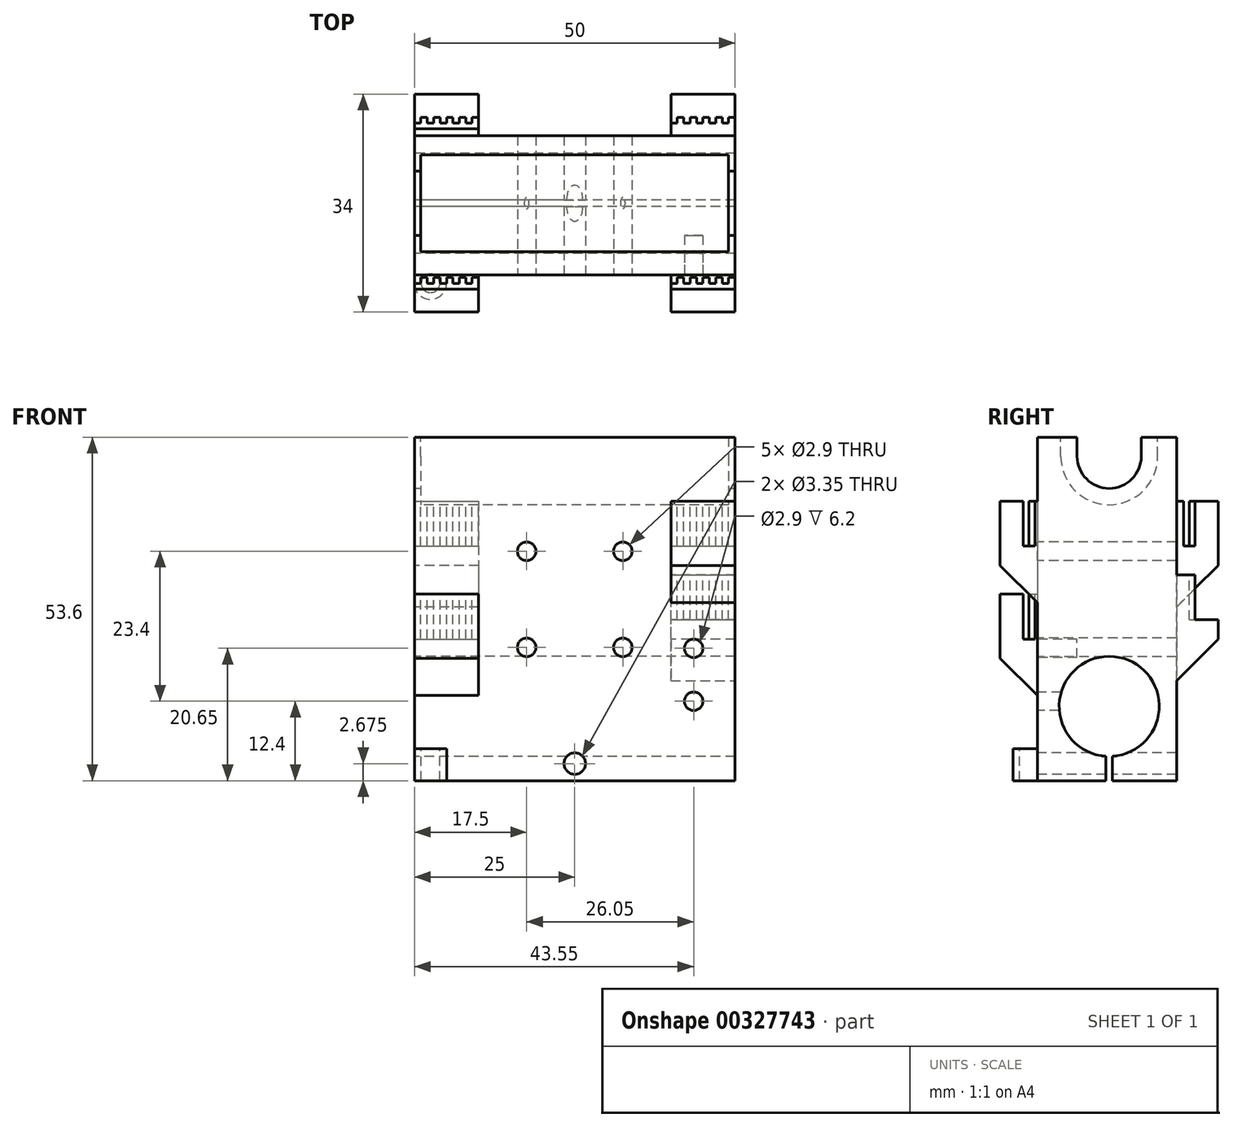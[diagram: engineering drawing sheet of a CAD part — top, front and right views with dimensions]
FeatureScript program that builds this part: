
annotation { "Feature Type Name" : "Feature", "Feature Type Description" : "" }
export const myFeature = defineFeature(function(context is Context, id is Id, definition is map)
    precondition{}
    {
        {
            var Q0;
            Q0=qCreatedBy(makeId("Top.planeOp"),FACE);
            var sketch = newSketch(context, id + "F0", { "sketchPlane" : qUnion([Q0])});
            skLineSegment(sketch, "E0.bottom", {"start": v(0, 0) * mm, "end": v(50, 0) * mm});
            skLineSegment(sketch, "E0.top", {"start": v(0, 20) * mm, "end": v(50, 20) * mm});
            skLineSegment(sketch, "E0.left", {"start": v(0, 0) * mm, "end": v(0, 20) * mm});
            skLineSegment(sketch, "E0.right", {"start": v(50, 0) * mm, "end": v(50, 20) * mm});
            skSolve(sketch);
        }
        {
            var Q0;
            Q0=qSketchRegion(id+"F0",true);
            extrude(context, id + "F1", {"entities" : qUnion([Q0]), "depth" : 50.6 * mm, "hasSecondDirection" : true, "secondDirectionOppositeDirection" : true, "secondDirectionDepth" : 3 * mm});
        }
        {
            var Q0;
            Q0=makeQuery(id+"F1.opExtrude","SWEPT_FACE",FACE,{"disambiguationData":[OSD([sQuery(id+"F0.wireOp",EDGE,"E0.left")])]});
            var sketch = newSketch(context, id + "F2", { "sketchPlane" : qUnion([Q0])});
            skCircle(sketch, "E1", {"center": v(-10, 8.6) * mm, "radius": 7.8 * mm});
            skCircle(sketch, "E2", {"center": v(-10, 47.6) * mm, "radius": 5 * mm});
            skLineSegment(sketch, "E3", {"start": v(-20, 47.6) * mm, "end": v(0, 47.6) * mm, "construction": true});
            skLineSegment(sketch, "E4", {"start": v(-15, 50.6) * mm, "end": v(-15, 47.6) * mm});
            skLineSegment(sketch, "E5", {"start": v(-5, 50.6) * mm, "end": v(-5, 47.6) * mm});
            skLineSegment(sketch, "E6", {"start": v(-20, 8.6) * mm, "end": v(0, 8.6) * mm, "construction": true});
            skLineSegment(sketch, "E7", {"start": v(-10, 8.6) * mm, "end": v(-10, -3) * mm, "construction": true});
            skLineSegment(sketch, "E8", {"start": v(-10, -3) * mm, "end": v(-10.5, -3) * mm});
            skLineSegment(sketch, "E9", {"start": v(-10.5, -3) * mm, "end": v(-10.5, 0.82) * mm});
            skLineSegment(sketch, "E10", {"start": v(-10.5, 0.82) * mm, "end": v(-9.5, 0.82) * mm});
            skLineSegment(sketch, "E11", {"start": v(-9.5, 0.82) * mm, "end": v(-9.5, 0) * mm});
            skLineSegment(sketch, "E12", {"start": v(-9.5, -3) * mm, "end": v(-10, -3) * mm});
            skLineSegment(sketch, "E13", {"start": v(-10, 15.6) * mm, "end": v(-10, 16.4) * mm});
            skLineSegment(sketch, "E14", {"start": v(-10, 15.6) * mm, "end": v(-5.38, 14.88) * mm});
            skLineSegment(sketch, "E15", {"start": v(-10, 15.6) * mm, "end": v(-14.62, 14.88) * mm});
            skCircle(sketch, "E16", {"center": v(-10, 47.6) * mm, "radius": 7.55 * mm});
            skLineSegment(sketch, "E17", {"start": v(-2.45, 47.6) * mm, "end": v(-2.45, 50.6) * mm});
            skLineSegment(sketch, "E18", {"start": v(-17.55, 47.6) * mm, "end": v(-17.55, 50.6) * mm});
            skLineSegment(sketch, "E19", {"start": v(-9.5, -3) * mm, "end": v(-9.5, 0) * mm});
            skSolve(sketch);
        }
        {
            var Q0;
            {var subQ0=sQuery(id+"F2.wireOp",EDGE,"E14");var subQ1=sQuery(id+"F2.wireOp",EDGE,"E1");var subQ3=makeQuery(id+"F2.imprint","INTERSECT",VERTEX,{"disambiguationData":[OD(0.0)],"derivedFrom":[subQ1,subQ0]});Q0=makeQuery(id+"F2.imprint","IMPRINT",FACE,{"disambiguationData":[TD([[makeQuery(id+"F2.imprint","IMPRINT",EDGE,{"disambiguationData":[TD([[subQ3,-1.0]])],"derivedFrom":subQ1}),1.0]])]});}
            var Q1;
            {var subQ0=sQuery(id+"F2.wireOp",EDGE,"E15");var subQ1=sQuery(id+"F2.wireOp",EDGE,"E1");var subQ3=makeQuery(id+"F2.imprint","INTERSECT",VERTEX,{"disambiguationData":[OD(0.0)],"derivedFrom":[subQ1,subQ0]});Q1=makeQuery(id+"F2.imprint","IMPRINT",FACE,{"disambiguationData":[TD([[makeQuery(id+"F2.imprint","IMPRINT",EDGE,{"disambiguationData":[TD([[subQ3,1.0]])],"derivedFrom":subQ1}),1.0]])]});}
            var Q2;
            Q2=makeQuery(id+"F2.imprint","IMPRINT",FACE,{"disambiguationData":[TD([[makeQuery(id+"F2.imprint","IMPRINT",EDGE,{"derivedFrom":sQuery(id+"F2.wireOp",EDGE,"E8")}),-1.0]])]});
            var Q3;
            {var subQ0=sQuery(id+"F2.wireOp",EDGE,"E10");Q3=makeQuery(id+"F2.imprint","IMPRINT",FACE,{"disambiguationData":[TD([[makeQuery(id+"F2.imprint","IMPRINT",EDGE,{"derivedFrom":subQ0}),-1.0]])]});}
            var Q4;
            {var subQ3=sQuery(id+"F2.wireOp",EDGE,"E13");Q4=makeQuery(id+"F2.imprint","IMPRINT",FACE,{"disambiguationData":[TD([[makeQuery(id+"F2.imprint","IMPRINT",EDGE,{"derivedFrom":subQ3}),-1.0]])]});}
            var Q5;
            {var subQ3=sQuery(id+"F2.wireOp",EDGE,"E13");Q5=makeQuery(id+"F2.imprint","IMPRINT",FACE,{"disambiguationData":[TD([[makeQuery(id+"F2.imprint","IMPRINT",EDGE,{"derivedFrom":subQ3}),1.0]])]});}
            var Q6;
            {var subQ7=sQuery(id+"F2.wireOp",EDGE,"E10");Q6=makeQuery(id+"F2.imprint","IMPRINT",FACE,{"disambiguationData":[TD([[makeQuery(id+"F2.imprint","IMPRINT",EDGE,{"derivedFrom":subQ7}),1.0]])]});}
            var Q7;
            {var subQ3=sQuery(id+"F2.wireOp",EDGE,"E5");Q7=makeQuery(id+"F2.imprint","IMPRINT",FACE,{"disambiguationData":[TD([[makeQuery(id+"F2.imprint","IMPRINT",EDGE,{"derivedFrom":subQ3}),-1.0]])]});}
            var Q8;
            {var subQ0=sQuery(id+"F2.wireOp",EDGE,"E4");Q8=makeQuery(id+"F2.imprint","IMPRINT",FACE,{"disambiguationData":[TD([[makeQuery(id+"F2.imprint","IMPRINT",EDGE,{"derivedFrom":subQ0}),1.0]])]});}
            var Q9;
            {var subQ0=sQuery(id+"F2.wireOp",EDGE,"E4");Q9=makeQuery(id+"F2.imprint","IMPRINT",FACE,{"disambiguationData":[TD([[makeQuery(id+"F2.imprint","IMPRINT",EDGE,{"derivedFrom":subQ0}),1.0]])]});}
            var Q10;
            {var subQ3=sQuery(id+"F2.wireOp",EDGE,"E5");Q10=makeQuery(id+"F2.imprint","IMPRINT",FACE,{"disambiguationData":[TD([[makeQuery(id+"F2.imprint","IMPRINT",EDGE,{"derivedFrom":subQ3}),-1.0]])]});}
            var Q11;
            {var subQ1=sQuery(id+"F2.wireOp",EDGE,"E2");var subQ4=makeQuery(id+"F2.imprint","INTERSECT",VERTEX,{"derivedFrom":[subQ1,sQuery(id+"F2.wireOp",EDGE,"E5")]});Q11=makeQuery(id+"F2.imprint","IMPRINT",FACE,{"disambiguationData":[TD([[makeQuery(id+"F2.imprint","IMPRINT",EDGE,{"disambiguationData":[TD([[subQ4,-1.0]])],"derivedFrom":subQ1}),1.0]])]});}
            extrude(context, id + "F3", {"entities" : qUnion([Q0, Q1, Q2, Q3, Q4, Q5, Q6, Q7, Q8, Q9, Q10, Q11]), "operationType" : NewBodyOperationType.REMOVE, "endBound" : BoundingType.THROUGH_ALL, "oppositeDirection" : true, "depth" : 25 * mm});
        }
        {
            var Q0;
            {var subQ3=sQuery(id+"F2.wireOp",EDGE,"E4");Q0=makeQuery(id+"F2.imprint","IMPRINT",FACE,{"disambiguationData":[TD([[makeQuery(id+"F2.imprint","IMPRINT",EDGE,{"derivedFrom":subQ3}),-1.0]])]});}
            var Q1;
            {var subQ3=sQuery(id+"F2.wireOp",EDGE,"E18");Q1=makeQuery(id+"F2.imprint","IMPRINT",FACE,{"disambiguationData":[TD([[makeQuery(id+"F2.imprint","IMPRINT",EDGE,{"derivedFrom":subQ3}),-1.0]])]});}
            var Q2;
            {var subQ3=sQuery(id+"F2.wireOp",EDGE,"E17");Q2=makeQuery(id+"F2.imprint","IMPRINT",FACE,{"disambiguationData":[TD([[makeQuery(id+"F2.imprint","IMPRINT",EDGE,{"derivedFrom":subQ3}),1.0]])]});}
            extrude(context, id + "F4", {"entities" : qUnion([Q0, Q1, Q2]), "operationType" : NewBodyOperationType.REMOVE, "oppositeDirection" : true, "depth" : 49 * mm});
        }
        {
            var Q0;
            {var subQ3=sQuery(id+"F2.wireOp",EDGE,"E4");Q0=makeQuery(id+"F2.imprint","IMPRINT",FACE,{"disambiguationData":[TD([[makeQuery(id+"F2.imprint","IMPRINT",EDGE,{"derivedFrom":subQ3}),-1.0]])]});}
            var Q1;
            {var subQ3=sQuery(id+"F2.wireOp",EDGE,"E18");Q1=makeQuery(id+"F2.imprint","IMPRINT",FACE,{"disambiguationData":[TD([[makeQuery(id+"F2.imprint","IMPRINT",EDGE,{"derivedFrom":subQ3}),-1.0]])]});}
            var Q2;
            {var subQ3=sQuery(id+"F2.wireOp",EDGE,"E17");Q2=makeQuery(id+"F2.imprint","IMPRINT",FACE,{"disambiguationData":[TD([[makeQuery(id+"F2.imprint","IMPRINT",EDGE,{"derivedFrom":subQ3}),1.0]])]});}
            extrude(context, id + "F5", {"entities" : qUnion([Q0, Q1, Q2]), "operationType" : NewBodyOperationType.ADD, "oppositeDirection" : true, "depth" : 16.21 * mm});
        }
        {
            var Q0;
            {var subQ3=sQuery(id+"F2.wireOp",EDGE,"E4");Q0=makeQuery(id+"F2.imprint","IMPRINT",FACE,{"disambiguationData":[TD([[makeQuery(id+"F2.imprint","IMPRINT",EDGE,{"derivedFrom":subQ3}),-1.0]])]});}
            var Q1;
            {var subQ3=sQuery(id+"F2.wireOp",EDGE,"E18");Q1=makeQuery(id+"F2.imprint","IMPRINT",FACE,{"disambiguationData":[TD([[makeQuery(id+"F2.imprint","IMPRINT",EDGE,{"derivedFrom":subQ3}),-1.0]])]});}
            var Q2;
            {var subQ3=sQuery(id+"F2.wireOp",EDGE,"E17");Q2=makeQuery(id+"F2.imprint","IMPRINT",FACE,{"disambiguationData":[TD([[makeQuery(id+"F2.imprint","IMPRINT",EDGE,{"derivedFrom":subQ3}),1.0]])]});}
            extrude(context, id + "F6", {"entities" : qUnion([Q0, Q1, Q2]), "operationType" : NewBodyOperationType.REMOVE, "oppositeDirection" : true, "depth" : 23.25 * mm});
        }
        {
            var Q0;
            {var subQ3=sQuery(id+"F2.wireOp",EDGE,"E4");Q0=makeQuery(id+"F2.imprint","IMPRINT",FACE,{"disambiguationData":[TD([[makeQuery(id+"F2.imprint","IMPRINT",EDGE,{"derivedFrom":subQ3}),-1.0]])]});}
            var Q1;
            {var subQ3=sQuery(id+"F2.wireOp",EDGE,"E18");Q1=makeQuery(id+"F2.imprint","IMPRINT",FACE,{"disambiguationData":[TD([[makeQuery(id+"F2.imprint","IMPRINT",EDGE,{"derivedFrom":subQ3}),-1.0]])]});}
            var Q2;
            {var subQ3=sQuery(id+"F2.wireOp",EDGE,"E17");Q2=makeQuery(id+"F2.imprint","IMPRINT",FACE,{"disambiguationData":[TD([[makeQuery(id+"F2.imprint","IMPRINT",EDGE,{"derivedFrom":subQ3}),1.0]])]});}
            extrude(context, id + "F7", {"entities" : qUnion([Q0, Q1, Q2]), "operationType" : NewBodyOperationType.ADD, "oppositeDirection" : true, "depth" : 1 * mm});
        }
        {
            var Q0;
            Q0=makeQuery(id+"F1.opExtrude","SWEPT_FACE",FACE,{"disambiguationData":[OSD([sQuery(id+"F0.wireOp",EDGE,"E0.bottom")])]});
            var sketch = newSketch(context, id + "F8", { "sketchPlane" : qUnion([Q0])});
            skLineSegment(sketch, "E20.bottom", {"start": v(0, 26.1) * mm, "end": v(10, 26.1) * mm});
            skLineSegment(sketch, "E20.top", {"start": v(0, 6.1) * mm, "end": v(10, 6.1) * mm});
            skLineSegment(sketch, "E20.left", {"start": v(0, 26.1) * mm, "end": v(0, 6.1) * mm});
            skLineSegment(sketch, "E20.right", {"start": v(10, 26.1) * mm, "end": v(10, 6.1) * mm});
            skLineSegment(sketch, "E21.bottom", {"start": v(50, 40.6) * mm, "end": v(40, 40.6) * mm});
            skLineSegment(sketch, "E21.top", {"start": v(50, 20.6) * mm, "end": v(40, 20.6) * mm});
            skLineSegment(sketch, "E21.left", {"start": v(50, 40.6) * mm, "end": v(50, 20.6) * mm});
            skLineSegment(sketch, "E21.right", {"start": v(40, 40.6) * mm, "end": v(40, 20.6) * mm});
            skPoint(sketch, "E22", {"position": v(0, 47.6) * mm});
            skPoint(sketch, "E23", {"position": v(0, 5.6) * mm});
            skSolve(sketch);
        }
        {
            var Q0;
            Q0=qSketchRegion(id+"F8",true);
            extrude(context, id + "F9", {"entities" : qUnion([Q0]), "operationType" : NewBodyOperationType.ADD, "depth" : 7 * mm});
        }
        {
            var Q0;
            Q0=makeQuery(id+"F9.opExtrude","SWEPT_FACE",FACE,{"disambiguationData":[OSD([sQuery(id+"F8.wireOp",EDGE,"E20.bottom")])]});
            var sketch = newSketch(context, id + "F10", { "sketchPlane" : qUnion([Q0])});
            skLineSegment(sketch, "E24", {"start": v(-935.9, 0) * mm, "end": v(-935.88, -4.54) * mm});
            skLineSegment(sketch, "E25.left", {"start": v(0, -3.4) * mm, "end": v(0, -1.6) * mm});
            skLineSegment(sketch, "E26", {"start": v(6, -2.5) * mm, "end": v(7, -2.5) * mm});
            skLineSegment(sketch, "E27", {"start": v(4, -2.5) * mm, "end": v(5, -2.5) * mm});
            skLineSegment(sketch, "E28", {"start": v(0, -2.5) * mm, "end": v(1, -2.5) * mm});
            skLineSegment(sketch, "E29", {"start": v(7, -1.6) * mm, "end": v(8, -1.6) * mm});
            skLineSegment(sketch, "E30", {"start": v(2, -2.5) * mm, "end": v(3, -2.5) * mm});
            skLineSegment(sketch, "E31", {"start": v(3, -1.6) * mm, "end": v(4, -1.6) * mm});
            skLineSegment(sketch, "E32", {"start": v(8, -2.5) * mm, "end": v(9, -2.5) * mm});
            skLineSegment(sketch, "E33", {"start": v(8, -1.6) * mm, "end": v(8, -2.5) * mm});
            skLineSegment(sketch, "E34", {"start": v(9, -2.5) * mm, "end": v(9, -1.6) * mm});
            skLineSegment(sketch, "E35", {"start": v(10, -1.6) * mm, "end": v(10, -2.5) * mm});
            skLineSegment(sketch, "E36", {"start": v(6, -1.6) * mm, "end": v(6, -2.5) * mm});
            skLineSegment(sketch, "E37", {"start": v(2, -1.6) * mm, "end": v(2, -2.5) * mm});
            skLineSegment(sketch, "E38", {"start": v(1, -1.6) * mm, "end": v(2, -1.6) * mm});
            skLineSegment(sketch, "E39", {"start": v(1, -2.5) * mm, "end": v(1, -1.6) * mm});
            skLineSegment(sketch, "E40", {"start": v(9, -1.6) * mm, "end": v(10, -1.6) * mm});
            skLineSegment(sketch, "E41", {"start": v(5, -1.6) * mm, "end": v(6, -1.6) * mm});
            skLineSegment(sketch, "E42", {"start": v(5, -2.5) * mm, "end": v(5, -1.6) * mm});
            skLineSegment(sketch, "E43", {"start": v(3, -2.5) * mm, "end": v(3, -1.6) * mm});
            skLineSegment(sketch, "E44", {"start": v(4, -1.6) * mm, "end": v(4, -2.5) * mm});
            skLineSegment(sketch, "E45", {"start": v(7, -2.5) * mm, "end": v(7, -1.6) * mm});
            skLineSegment(sketch, "E46", {"start": v(0, -1.6) * mm, "end": v(0, -2.5) * mm});
            skLineSegment(sketch, "E47", {"start": v(10, -2.5) * mm, "end": v(10, -3.4) * mm});
            skLineSegment(sketch, "E48", {"start": v(0, -3.4) * mm, "end": v(10, -3.4) * mm});
            skLineSegment(sketch, "E49", {"start": v(5.3, -1.6) * mm, "end": v(5.3, 0) * mm});
            skSolve(sketch);
        }
        {
            var Q0;
            Q0=qSketchRegion(id+"F10",true);
            extrude(context, id + "F11", {"entities" : qUnion([Q0]), "operationType" : NewBodyOperationType.REMOVE, "oppositeDirection" : true, "depth" : 7 * mm});
        }
        {
            var Q0;
            Q0=makeQuery(id+"F9.opExtrude","SWEPT_FACE",FACE,{"disambiguationData":[OSD([sQuery(id+"F8.wireOp",EDGE,"E21.bottom")])]});
            var sketch = newSketch(context, id + "F12", { "sketchPlane" : qUnion([Q0])});
            skLineSegment(sketch, "E50.left", {"start": v(40, -3.4) * mm, "end": v(40, -1.6) * mm});
            skLineSegment(sketch, "E51", {"start": v(46, -2.5) * mm, "end": v(47, -2.5) * mm});
            skLineSegment(sketch, "E52", {"start": v(44, -2.5) * mm, "end": v(45, -2.5) * mm});
            skLineSegment(sketch, "E53", {"start": v(40, -2.5) * mm, "end": v(41, -2.5) * mm});
            skLineSegment(sketch, "E54", {"start": v(47, -1.6) * mm, "end": v(48, -1.6) * mm});
            skLineSegment(sketch, "E55", {"start": v(42, -2.5) * mm, "end": v(43, -2.5) * mm});
            skLineSegment(sketch, "E56", {"start": v(43, -1.6) * mm, "end": v(44, -1.6) * mm});
            skLineSegment(sketch, "E57", {"start": v(48, -2.5) * mm, "end": v(49, -2.5) * mm});
            skLineSegment(sketch, "E58", {"start": v(48, -1.6) * mm, "end": v(48, -2.5) * mm});
            skLineSegment(sketch, "E59", {"start": v(49, -2.5) * mm, "end": v(49, -1.6) * mm});
            skLineSegment(sketch, "E60", {"start": v(50, -1.6) * mm, "end": v(50, -2.5) * mm});
            skLineSegment(sketch, "E61", {"start": v(46, -1.6) * mm, "end": v(46, -2.5) * mm});
            skLineSegment(sketch, "E62", {"start": v(42, -1.6) * mm, "end": v(42, -2.5) * mm});
            skLineSegment(sketch, "E63", {"start": v(41, -1.6) * mm, "end": v(42, -1.6) * mm});
            skLineSegment(sketch, "E64", {"start": v(41, -2.5) * mm, "end": v(41, -1.6) * mm});
            skLineSegment(sketch, "E65", {"start": v(49, -1.6) * mm, "end": v(50, -1.6) * mm});
            skLineSegment(sketch, "E66", {"start": v(45, -1.6) * mm, "end": v(46, -1.6) * mm});
            skLineSegment(sketch, "E67", {"start": v(45, -2.5) * mm, "end": v(45, -1.6) * mm});
            skLineSegment(sketch, "E68", {"start": v(43, -2.5) * mm, "end": v(43, -1.6) * mm});
            skLineSegment(sketch, "E69", {"start": v(44, -1.6) * mm, "end": v(44, -2.5) * mm});
            skLineSegment(sketch, "E70", {"start": v(47, -2.5) * mm, "end": v(47, -1.6) * mm});
            skLineSegment(sketch, "E71", {"start": v(40, -1.6) * mm, "end": v(40, -2.5) * mm});
            skLineSegment(sketch, "E72", {"start": v(50, -2.5) * mm, "end": v(50, -3.4) * mm});
            skLineSegment(sketch, "E73", {"start": v(40, -3.4) * mm, "end": v(50, -3.4) * mm});
            skLineSegment(sketch, "E74", {"start": v(45.23, -1.6) * mm, "end": v(45.23, 0) * mm});
            skSolve(sketch);
        }
        {
            var Q0;
            Q0=qSketchRegion(id+"F12",true);
            extrude(context, id + "F13", {"entities" : qUnion([Q0]), "operationType" : NewBodyOperationType.REMOVE, "oppositeDirection" : true, "depth" : 7 * mm});
        }
        {
            var Q0;
            Q0=makeQuery(id+"F1.opExtrude","SWEPT_FACE",FACE,{"disambiguationData":[OSD([sQuery(id+"F0.wireOp",EDGE,"E0.top")])]});
            var sketch = newSketch(context, id + "F14", { "sketchPlane" : qUnion([Q0])});
            skLineSegment(sketch, "E75.bottom", {"start": v(-50, 9.1) * mm, "end": v(-40, 9.1) * mm});
            skLineSegment(sketch, "E75.top", {"start": v(-50, 29.1) * mm, "end": v(-40, 29.1) * mm});
            skLineSegment(sketch, "E75.left", {"start": v(-50, 9.1) * mm, "end": v(-50, 29.1) * mm});
            skLineSegment(sketch, "E75.right", {"start": v(-40, 9.1) * mm, "end": v(-40, 29.1) * mm});
            skLineSegment(sketch, "E76.bottom", {"start": v(0, 40.6) * mm, "end": v(-10, 40.6) * mm});
            skLineSegment(sketch, "E76.top", {"start": v(0, 20.6) * mm, "end": v(-10, 20.6) * mm});
            skLineSegment(sketch, "E76.left", {"start": v(0, 40.6) * mm, "end": v(0, 20.6) * mm});
            skLineSegment(sketch, "E76.right", {"start": v(-10, 40.6) * mm, "end": v(-10, 20.6) * mm});
            skSolve(sketch);
        }
        {
            var Q0;
            Q0=qSketchRegion(id+"F14",true);
            extrude(context, id + "F15", {"entities" : qUnion([Q0]), "operationType" : NewBodyOperationType.ADD, "depth" : 7 * mm});
        }
        {
            var Q0;
            Q0=makeQuery(id+"F15.opExtrude","SWEPT_FACE",FACE,{"disambiguationData":[OSD([sQuery(id+"F14.wireOp",EDGE,"E75.top")])]});
            var sketch = newSketch(context, id + "F16", { "sketchPlane" : qUnion([Q0])});
            skLineSegment(sketch, "E77.left", {"start": v(40, 21.6) * mm, "end": v(40, 23.4) * mm});
            skLineSegment(sketch, "E78", {"start": v(46, 22.5) * mm, "end": v(47, 22.5) * mm});
            skLineSegment(sketch, "E79", {"start": v(44, 22.5) * mm, "end": v(45, 22.5) * mm});
            skLineSegment(sketch, "E80", {"start": v(40, 22.5) * mm, "end": v(41, 22.5) * mm});
            skLineSegment(sketch, "E81", {"start": v(47, 23.4) * mm, "end": v(48, 23.4) * mm});
            skLineSegment(sketch, "E82", {"start": v(42, 22.5) * mm, "end": v(43, 22.5) * mm});
            skLineSegment(sketch, "E83", {"start": v(43, 23.4) * mm, "end": v(44, 23.4) * mm});
            skLineSegment(sketch, "E84", {"start": v(48, 22.5) * mm, "end": v(49, 22.5) * mm});
            skLineSegment(sketch, "E85", {"start": v(48, 23.4) * mm, "end": v(48, 22.5) * mm});
            skLineSegment(sketch, "E86", {"start": v(49, 22.5) * mm, "end": v(49, 23.4) * mm});
            skLineSegment(sketch, "E87", {"start": v(50, 23.4) * mm, "end": v(50, 22.5) * mm});
            skLineSegment(sketch, "E88", {"start": v(46, 23.4) * mm, "end": v(46, 22.5) * mm});
            skLineSegment(sketch, "E89", {"start": v(42, 23.4) * mm, "end": v(42, 22.5) * mm});
            skLineSegment(sketch, "E90", {"start": v(41, 23.4) * mm, "end": v(42, 23.4) * mm});
            skLineSegment(sketch, "E91", {"start": v(41, 22.5) * mm, "end": v(41, 23.4) * mm});
            skLineSegment(sketch, "E92", {"start": v(49, 23.4) * mm, "end": v(50, 23.4) * mm});
            skLineSegment(sketch, "E93", {"start": v(45, 23.4) * mm, "end": v(46, 23.4) * mm});
            skLineSegment(sketch, "E94", {"start": v(45, 22.5) * mm, "end": v(45, 23.4) * mm});
            skLineSegment(sketch, "E95", {"start": v(43, 22.5) * mm, "end": v(43, 23.4) * mm});
            skLineSegment(sketch, "E96", {"start": v(44, 23.4) * mm, "end": v(44, 22.5) * mm});
            skLineSegment(sketch, "E97", {"start": v(47, 22.5) * mm, "end": v(47, 23.4) * mm});
            skLineSegment(sketch, "E98", {"start": v(40, 23.4) * mm, "end": v(40, 22.5) * mm});
            skLineSegment(sketch, "E99", {"start": v(50, 22.5) * mm, "end": v(50, 21.6) * mm});
            skLineSegment(sketch, "E100", {"start": v(40, 21.6) * mm, "end": v(50, 21.6) * mm});
            skLineSegment(sketch, "E101", {"start": v(45, 21.6) * mm, "end": v(45, 20) * mm});
            skSolve(sketch);
        }
        {
            var Q0;
            {var subQ4=sQuery(id+"F16.wireOp",EDGE,"E77.left");Q0=makeQuery(id+"F16.imprint","IMPRINT",FACE,{"disambiguationData":[TD([[makeQuery(id+"F16.imprint","IMPRINT",EDGE,{"derivedFrom":subQ4}),1.0]])]});}
            extrude(context, id + "F17", {"entities" : qUnion([Q0]), "operationType" : NewBodyOperationType.REMOVE, "oppositeDirection" : true, "depth" : 7 * mm});
        }
        {
            var Q0;
            Q0=makeQuery(id+"F15.opExtrude","SWEPT_FACE",FACE,{"disambiguationData":[OSD([sQuery(id+"F14.wireOp",EDGE,"E76.bottom")])]});
            var sketch = newSketch(context, id + "F18", { "sketchPlane" : qUnion([Q0])});
            skLineSegment(sketch, "E102", {"start": v(6, 22.5) * mm, "end": v(7, 22.5) * mm});
            skLineSegment(sketch, "E103", {"start": v(4, 22.5) * mm, "end": v(5, 22.5) * mm});
            skLineSegment(sketch, "E104", {"start": v(0, 22.5) * mm, "end": v(1, 22.5) * mm});
            skLineSegment(sketch, "E105", {"start": v(7, 23.4) * mm, "end": v(8, 23.4) * mm});
            skLineSegment(sketch, "E106", {"start": v(2, 22.5) * mm, "end": v(3, 22.5) * mm});
            skLineSegment(sketch, "E107", {"start": v(3, 23.4) * mm, "end": v(4, 23.4) * mm});
            skLineSegment(sketch, "E108", {"start": v(8, 22.5) * mm, "end": v(9, 22.5) * mm});
            skLineSegment(sketch, "E109", {"start": v(8, 23.4) * mm, "end": v(8, 22.5) * mm});
            skLineSegment(sketch, "E110", {"start": v(9, 22.5) * mm, "end": v(9, 23.4) * mm});
            skLineSegment(sketch, "E111", {"start": v(10, 23.4) * mm, "end": v(10, 22.5) * mm});
            skLineSegment(sketch, "E112", {"start": v(6, 23.4) * mm, "end": v(6, 22.5) * mm});
            skLineSegment(sketch, "E113", {"start": v(2, 23.4) * mm, "end": v(2, 22.5) * mm});
            skLineSegment(sketch, "E114", {"start": v(1, 23.4) * mm, "end": v(2, 23.4) * mm});
            skLineSegment(sketch, "E115", {"start": v(1, 22.5) * mm, "end": v(1, 23.4) * mm});
            skLineSegment(sketch, "E116", {"start": v(9, 23.4) * mm, "end": v(10, 23.4) * mm});
            skLineSegment(sketch, "E117", {"start": v(5, 23.4) * mm, "end": v(6, 23.4) * mm});
            skLineSegment(sketch, "E118", {"start": v(5, 22.5) * mm, "end": v(5, 23.4) * mm});
            skLineSegment(sketch, "E119", {"start": v(3, 22.5) * mm, "end": v(3, 23.4) * mm});
            skLineSegment(sketch, "E120", {"start": v(4, 23.4) * mm, "end": v(4, 22.5) * mm});
            skLineSegment(sketch, "E121", {"start": v(7, 22.5) * mm, "end": v(7, 23.4) * mm});
            skLineSegment(sketch, "E122", {"start": v(10, 22.5) * mm, "end": v(10, 21.6) * mm});
            skLineSegment(sketch, "E123", {"start": v(0, 21.6) * mm, "end": v(10, 21.6) * mm});
            skLineSegment(sketch, "E124", {"start": v(5, 21.6) * mm, "end": v(5, 20) * mm});
            skLineSegment(sketch, "E125", {"start": v(0, 21.6) * mm, "end": v(0, 22.5) * mm});
            skSolve(sketch);
        }
        {
            var Q0;
            Q0=makeQuery(id+"F18.imprint","IMPRINT",FACE,{"disambiguationData":[TD([[makeQuery(id+"F18.imprint","IMPRINT",EDGE,{"derivedFrom":sQuery(id+"F18.wireOp",EDGE,"E102")}),-1.0]])]});
            extrude(context, id + "F19", {"entities" : qUnion([Q0]), "operationType" : NewBodyOperationType.REMOVE, "oppositeDirection" : true, "depth" : 7 * mm});
        }
        {
            var Q0;
            Q0=makeQuery(id+"F1.opExtrude","SWEPT_FACE",FACE,{"disambiguationData":[OSD([sQuery(id+"F0.wireOp",EDGE,"E0.bottom")])]});
            var sketch = newSketch(context, id + "F20", { "sketchPlane" : qUnion([Q0])});
            skCircle(sketch, "E126", {"center": v(17.5, 32.8) * mm, "radius": 1.45 * mm});
            skCircle(sketch, "E127", {"center": v(32.5, 32.8) * mm, "radius": 1.45 * mm});
            skCircle(sketch, "E128", {"center": v(17.5, 17.8) * mm, "radius": 1.45 * mm});
            skCircle(sketch, "E129", {"center": v(32.5, 17.8) * mm, "radius": 1.45 * mm});
            skLineSegment(sketch, "E130", {"start": v(17.5, 32.8) * mm, "end": v(0, 32.8) * mm});
            skLineSegment(sketch, "E131", {"start": v(32.5, 17.8) * mm, "end": v(50, 17.8) * mm});
            skLineSegment(sketch, "E132", {"start": v(32.5, 32.8) * mm, "end": v(32.5, 50.6) * mm});
            skLineSegment(sketch, "E133", {"start": v(17.5, 17.8) * mm, "end": v(17.5, 0) * mm});
            skCircle(sketch, "E134", {"center": v(25, -0.32) * mm, "radius": 1.68 * mm});
            skLineSegment(sketch, "E135", {"start": v(25, -3) * mm, "end": v(25, 13.82) * mm, "construction": true});
            skSolve(sketch);
        }
        {
            var Q0;
            Q0=qSketchRegion(id+"F20",true);
            var Q1;
            Q1=makeQuery(id+"F20.imprint","IMPRINT",FACE,{"disambiguationData":[TD([[makeQuery(id+"F20.imprint","IMPRINT",EDGE,{"derivedFrom":sQuery(id+"F20.wireOp",EDGE,"E126")}),1.0]])]});
            var Q2;
            Q2=makeQuery(id+"F20.imprint","IMPRINT",FACE,{"disambiguationData":[TD([[makeQuery(id+"F20.imprint","IMPRINT",EDGE,{"derivedFrom":sQuery(id+"F20.wireOp",EDGE,"E127")}),1.0]])]});
            var Q3;
            Q3=makeQuery(id+"F20.imprint","IMPRINT",FACE,{"disambiguationData":[TD([[makeQuery(id+"F20.imprint","IMPRINT",EDGE,{"derivedFrom":sQuery(id+"F20.wireOp",EDGE,"E129")}),1.0]])]});
            var Q4;
            Q4=makeQuery(id+"F20.imprint","IMPRINT",FACE,{"disambiguationData":[TD([[makeQuery(id+"F20.imprint","IMPRINT",EDGE,{"derivedFrom":sQuery(id+"F20.wireOp",EDGE,"E128")}),1.0]])]});
            extrude(context, id + "F21", {"entities" : qUnion([Q0, Q1, Q2, Q3, Q4]), "operationType" : NewBodyOperationType.REMOVE, "endBound" : BoundingType.THROUGH_ALL, "oppositeDirection" : true, "depth" : 25 * mm});
        }
        {
            var Q0;
            Q0=makeQuery(id+"F1.opExtrude","SWEPT_FACE",FACE,{"disambiguationData":[OSD([sQuery(id+"F0.wireOp",EDGE,"E0.bottom")])]});
            var sketch = newSketch(context, id + "F22", { "sketchPlane" : qUnion([Q0])});
            skCircle(sketch, "E136", {"center": v(43.55, 17.65) * mm, "radius": 1.45 * mm});
            skCircle(sketch, "E137", {"center": v(43.55, 9.4) * mm, "radius": 1.45 * mm});
            skSolve(sketch);
        }
        {
            var Q0;
            Q0=qSketchRegion(id+"F22",true);
            extrude(context, id + "F23", {"entities" : qUnion([Q0]), "operationType" : NewBodyOperationType.REMOVE, "oppositeDirection" : true, "depth" : 5 * mm});
        }
        {
            var Q0;
            Q0=makeQuery(id+"F1.opExtrude","SWEPT_FACE",FACE,{"disambiguationData":[OSD([sQuery(id+"F0.wireOp",EDGE,"E0.bottom")])]});
            var sketch = newSketch(context, id + "F24", { "sketchPlane" : qUnion([Q0])});
            skLineSegment(sketch, "E138.bottom", {"start": v(0, -3) * mm, "end": v(5, -3) * mm});
            skLineSegment(sketch, "E138.top", {"start": v(0, 2) * mm, "end": v(5, 2) * mm});
            skLineSegment(sketch, "E138.left", {"start": v(0, -3) * mm, "end": v(0, 2) * mm});
            skLineSegment(sketch, "E138.right", {"start": v(5, -3) * mm, "end": v(5, 2) * mm});
            skSolve(sketch);
        }
        {
            var Q0;
            Q0=qSketchRegion(id+"F24",true);
            extrude(context, id + "F25", {"entities" : qUnion([Q0]), "operationType" : NewBodyOperationType.ADD, "depth" : 5 * mm});
        }
        {
            var Q0;
            Q0=makeQuery(id+"F25.opExtrude","SWEPT_FACE",FACE,{"disambiguationData":[OSD([sQuery(id+"F24.wireOp",EDGE,"E138.top")])]});
            var sketch = newSketch(context, id + "F26", { "sketchPlane" : qUnion([Q0])});
            skCircle(sketch, "E139", {"center": v(2.5, -2.5) * mm, "radius": 1.45 * mm});
            skLineSegment(sketch, "E140", {"start": v(0, -2.5) * mm, "end": v(5, -2.5) * mm});
            skSolve(sketch);
        }
        {
            var Q0;
            Q0=qSketchRegion(id+"F26",true);
            extrude(context, id + "F27", {"entities" : qUnion([Q0]), "operationType" : NewBodyOperationType.REMOVE, "oppositeDirection" : true, "depth" : 25 * mm});
        }
        {
            var Q0;
            Q0=makeQuery(id+"F25.opExtrude","CAP_EDGE",EDGE,{"disambiguationData":[OSD([sQuery(id+"F24.wireOp",EDGE,"E138.left")])],"isStart":false});
            var Q1;
            Q1=makeQuery(id+"F25.opExtrude","CAP_EDGE",EDGE,{"disambiguationData":[OSD([sQuery(id+"F24.wireOp",EDGE,"E138.right")])],"isStart":false});
            fillet(context, id + "F28", {"entities" : qUnion([Q0, Q1]), "radius" : 2.5 * mm, "tangentPropagation" : true, "allowEdgeOverflow" : false});
        }
        {
            var Q0;
            Q0=makeQuery(id+"F1.opExtrude","SWEPT_FACE",FACE,{"disambiguationData":[OSD([sQuery(id+"F0.wireOp",EDGE,"E0.top")])]});
            var sketch = newSketch(context, id + "F29", { "sketchPlane" : qUnion([Q0])});
            skSolve(sketch);
        }
        {
            var Q0;
            Q0=qSketchRegion(id+"F29",true);
            var Q1;
            {var subQ0=sQuery(id+"F0.wireOp",EDGE,"E0.top");Q1=makeQuery(id+"F29.imprint","IMPRINT",FACE,{"disambiguationData":[TD([[makeQuery(id+"F29.imprint","IMPRINT",EDGE,{"derivedFrom":makeQuery(id+"F1.opExtrude","CAP_EDGE",EDGE,{"disambiguationData":[OSD([subQ0])],"isStart":true})}),-1.0]])]});}
            var Q2;
            Q2=makeQuery(id+"F17.boolean.opBoolean","COPY",FACE,{"derivedFrom":makeQuery(id+"F17.opExtrude","SWEPT_FACE",FACE,{"disambiguationData":[OSD([sQuery(id+"F16.wireOp",EDGE,"E100")])]})});
            var Q3;
            Q3=makeQuery(id+"F1.opExtrude","SWEPT_BODY",BODY,{"disambiguationData":[OSD([sQuery(id+"F0.wireOp",EDGE,"E0.bottom"),sQuery(id+"F0.wireOp",EDGE,"E0.top"),sQuery(id+"F0.wireOp",EDGE,"E0.left"),sQuery(id+"F0.wireOp",EDGE,"E0.right")])]});
            extrude(context, id + "F30", {"entities" : qUnion([Q0, Q1]), "operationType" : NewBodyOperationType.ADD, "endBoundEntityFace" : qUnion([Q2]), "endBoundEntityBody" : qUnion([Q3]), "depth" : .5 * mm});
        }
        {
            var Q0;
            Q0=makeQuery(id+"F1.opExtrude","SWEPT_FACE",FACE,{"disambiguationData":[OSD([sQuery(id+"F0.wireOp",EDGE,"E0.bottom")])]});
            var Q1;
            Q1=makeQuery(id+"F13.boolean.opBoolean","COPY",FACE,{"derivedFrom":makeQuery(id+"F13.opExtrude","SWEPT_FACE",FACE,{"disambiguationData":[OSD([sQuery(id+"F12.wireOp",EDGE,"E65")])]})});
            extrude(context, id + "F31", {"entities" : qUnion([Q0]), "operationType" : NewBodyOperationType.ADD, "endBoundEntityFace" : qUnion([Q1]), "depth" : 1.2 * mm});
        }
        {
            var Q0;
            Q0=makeQuery(id+"F9.opExtrude","CAP_EDGE",EDGE,{"disambiguationData":[OSD([sQuery(id+"F8.wireOp",EDGE,"E20.top")])],"isStart":false});
            var Q1;
            Q1=makeQuery(id+"F9.opExtrude","CAP_EDGE",EDGE,{"disambiguationData":[OSD([sQuery(id+"F8.wireOp",EDGE,"E21.top")])],"isStart":false});
            chamfer(context, id + "F32", {"entities" : qUnion([Q0, Q1]), "width" : 10 * mm, "tangentPropagation" : true});
        }
        {
            var Q0;
            Q0=makeQuery(id+"F15.opExtrude","CAP_EDGE",EDGE,{"disambiguationData":[OSD([sQuery(id+"F14.wireOp",EDGE,"E75.bottom")])],"isStart":false});
            var Q1;
            Q1=makeQuery(id+"F15.opExtrude","CAP_EDGE",EDGE,{"disambiguationData":[OSD([sQuery(id+"F14.wireOp",EDGE,"E76.top")])],"isStart":false});
            chamfer(context, id + "F33", {"entities" : qUnion([Q0, Q1]), "width" : 10 * mm, "tangentPropagation" : true});
        }
    });
